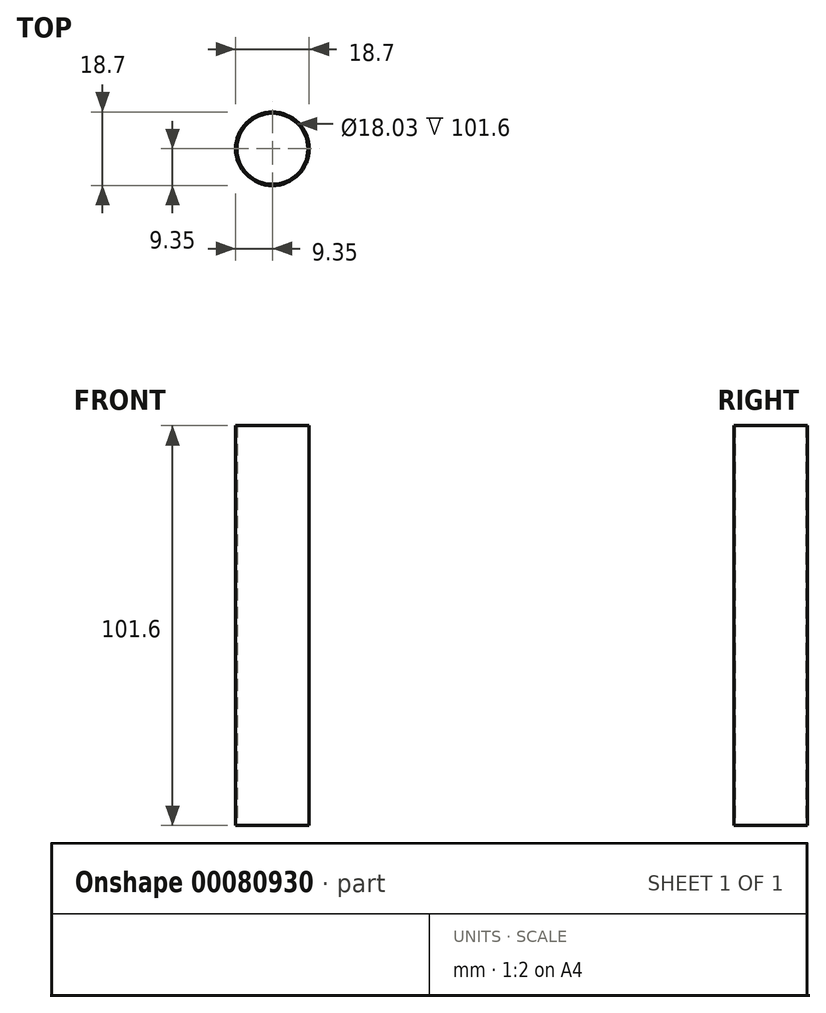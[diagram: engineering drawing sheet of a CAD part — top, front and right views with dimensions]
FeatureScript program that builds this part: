
annotation { "Feature Type Name" : "Feature", "Feature Type Description" : "" }
export const myFeature = defineFeature(function(context is Context, id is Id, definition is map)
    precondition{}
    {
        {
            var Q0;
            Q0=qCreatedBy(makeId("Top.planeOp"),FACE);
            var sketch = newSketch(context, id + "F0", { "sketchPlane" : qUnion([Q0])});
            skCircle(sketch, "E0", {"center": v(0, 0) * mm, "radius": 9.35 * mm});
            skCircle(sketch, "E1", {"center": v(0, 0) * mm, "radius": 9.02 * mm});
            skSolve(sketch);
        }
        {
            var Q0;
            Q0=makeQuery(id+"F0.imprint","IMPRINT",FACE,{"disambiguationData":[TD([[makeQuery(id+"F0.imprint","IMPRINT",EDGE,{"derivedFrom":sQuery(id+"F0.wireOp",EDGE,"E0")}),1.0]])]});
            extrude(context, id + "F1", {"entities" : qUnion([Q0]), "depth" : 101.6 * mm});
        }
    });
